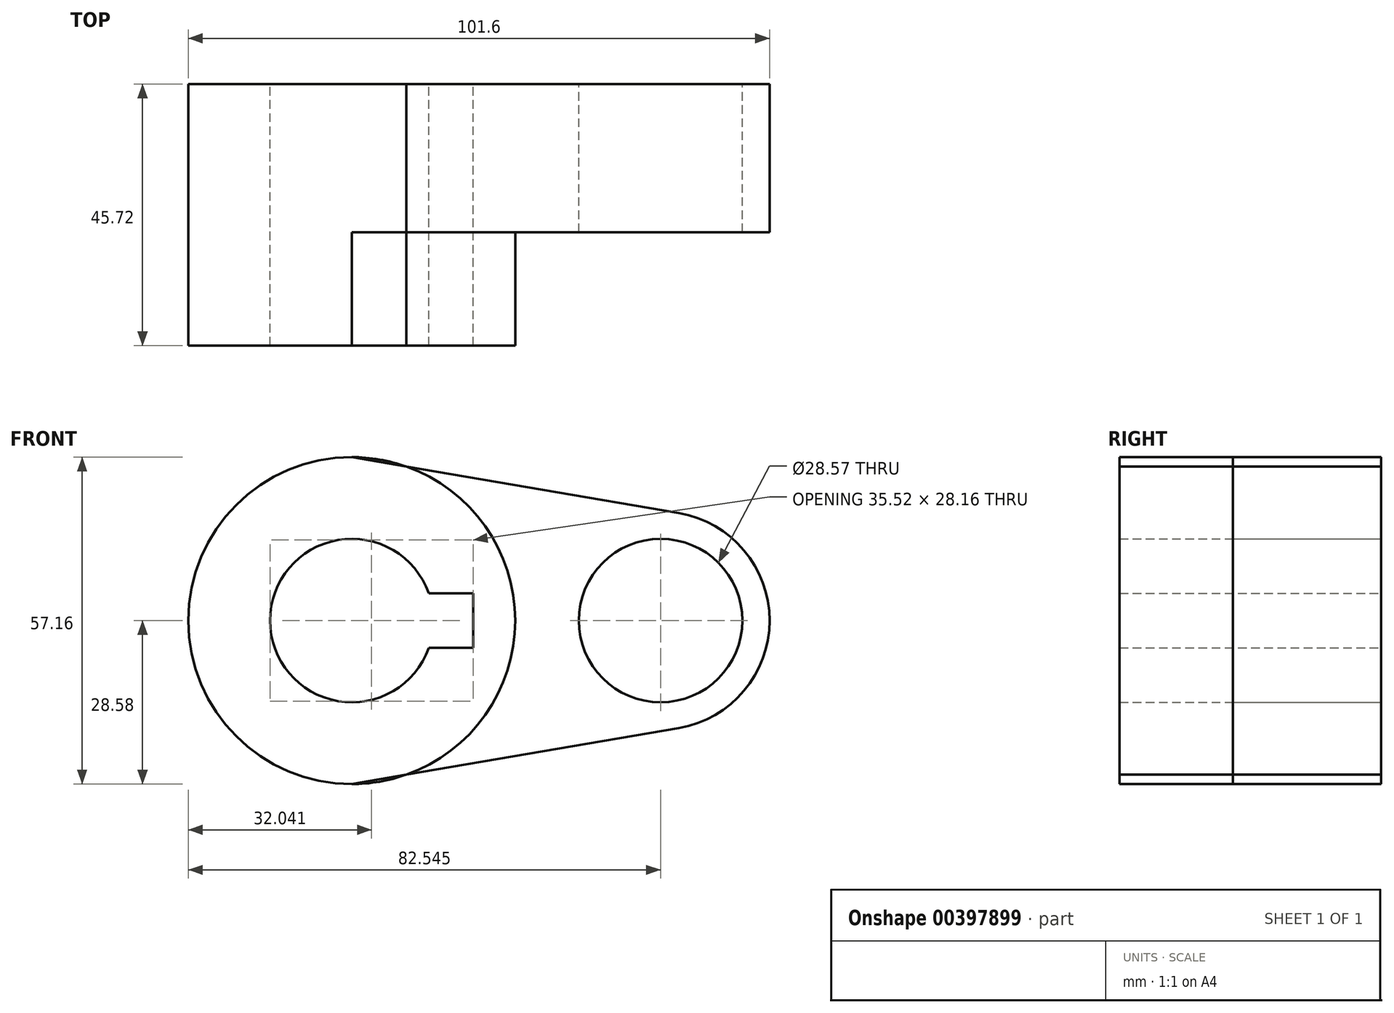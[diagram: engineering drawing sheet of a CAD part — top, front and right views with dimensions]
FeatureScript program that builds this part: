
annotation { "Feature Type Name" : "Feature", "Feature Type Description" : "" }
export const myFeature = defineFeature(function(context is Context, id is Id, definition is map)
    precondition{}
    {
        {
            var Q0;
            Q0=qCreatedBy(makeId("Front.planeOp"),FACE);
            var sketch = newSketch(context, id + "F0", { "sketchPlane" : qUnion([Q0])});
            skCircle(sketch, "E0", {"center": v(0, 0) * mm, "radius": 28.58 * mm});
            skCircle(sketch, "E1", {"center": v(53.98, 0) * mm, "radius": 19.05 * mm});
            skLineSegment(sketch, "E2", {"start": v(0, 28.57) * mm, "end": v(57.2, 18.78) * mm});
            skLineSegment(sketch, "E3", {"start": v(0, -28.58) * mm, "end": v(57.2, -18.78) * mm});
            skCircle(sketch, "E4", {"center": v(0, 0) * mm, "radius": 14.29 * mm});
            skCircle(sketch, "E5", {"center": v(53.98, 0) * mm, "radius": 14.29 * mm});
            skLineSegment(sketch, "E6.bottom", {"start": v(21.23, -4.76) * mm, "end": v(-16.87, -4.76) * mm});
            skLineSegment(sketch, "E6.top", {"start": v(21.23, 4.76) * mm, "end": v(-16.87, 4.76) * mm});
            skLineSegment(sketch, "E6.left", {"start": v(21.23, -4.76) * mm, "end": v(21.23, 4.76) * mm});
            skLineSegment(sketch, "E6.right", {"start": v(-16.87, -4.76) * mm, "end": v(-16.87, 4.76) * mm});
            skPoint(sketch, "E6.middle", {"position": v(2.18, 0) * mm});
            skSolve(sketch);
        }
        {
            var Q0;
            {var subQ5=sQuery(id+"F0.wireOp",EDGE,"E6.right");Q0=makeQuery(id+"F0.imprint","IMPRINT",FACE,{"disambiguationData":[TD([[makeQuery(id+"F0.imprint","IMPRINT",EDGE,{"derivedFrom":subQ5}),-1.0]])]});}
            var Q1;
            {var subQ4=sQuery(id+"F0.wireOp",EDGE,"E6.left");Q1=makeQuery(id+"F0.imprint","IMPRINT",FACE,{"disambiguationData":[TD([[makeQuery(id+"F0.imprint","IMPRINT",EDGE,{"derivedFrom":subQ4}),-1.0]])]});}
            extrude(context, id + "F1", {"entities" : qUnion([Q0, Q1]), "depth" : 45.72 * mm});
        }
        {
            var Q0;
            Q0 = qSketchRegion(id + "F0", true);
            extrude(context, id + "F2", {"entities" : qUnion([Q0]), "operationType" : NewBodyOperationType.ADD, "depth" : 25.9 * mm});
        }
    });
